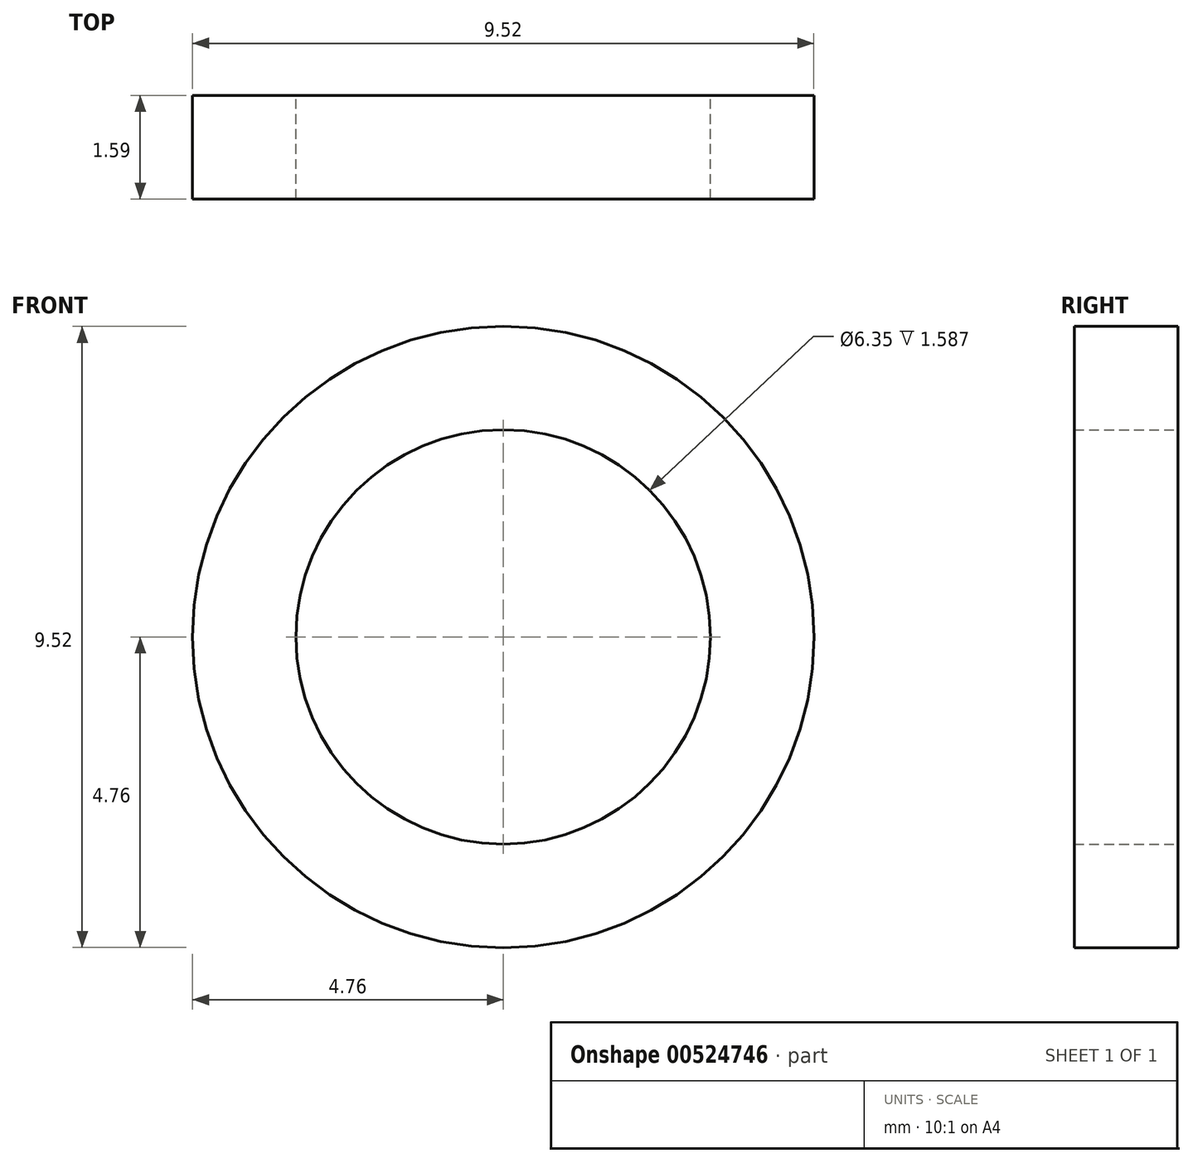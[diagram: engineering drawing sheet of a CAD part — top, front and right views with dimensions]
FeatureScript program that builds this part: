
annotation { "Feature Type Name" : "Feature", "Feature Type Description" : "" }
export const myFeature = defineFeature(function(context is Context, id is Id, definition is map)
    precondition{}
    {
        {
            var Q0;
            Q0=qCreatedBy(makeId("Front.planeOp"),FACE);
            var sketch = newSketch(context, id + "F0", { "sketchPlane" : qUnion([Q0])});
            skCircle(sketch, "E0", {"center": v(0, 0) * mm, "radius": 3.18 * mm});
            skCircle(sketch, "E1", {"center": v(0, 0) * mm, "radius": 4.76 * mm});
            skSolve(sketch);
        }
        {
            var Q0;
            Q0 = qSketchRegion(id + "F0", true);
            extrude(context, id + "F1", {"entities" : qUnion([Q0]), "depth" : 1.59 * mm, "offsetDistance" : 25.4 * mm});
        }
    });
